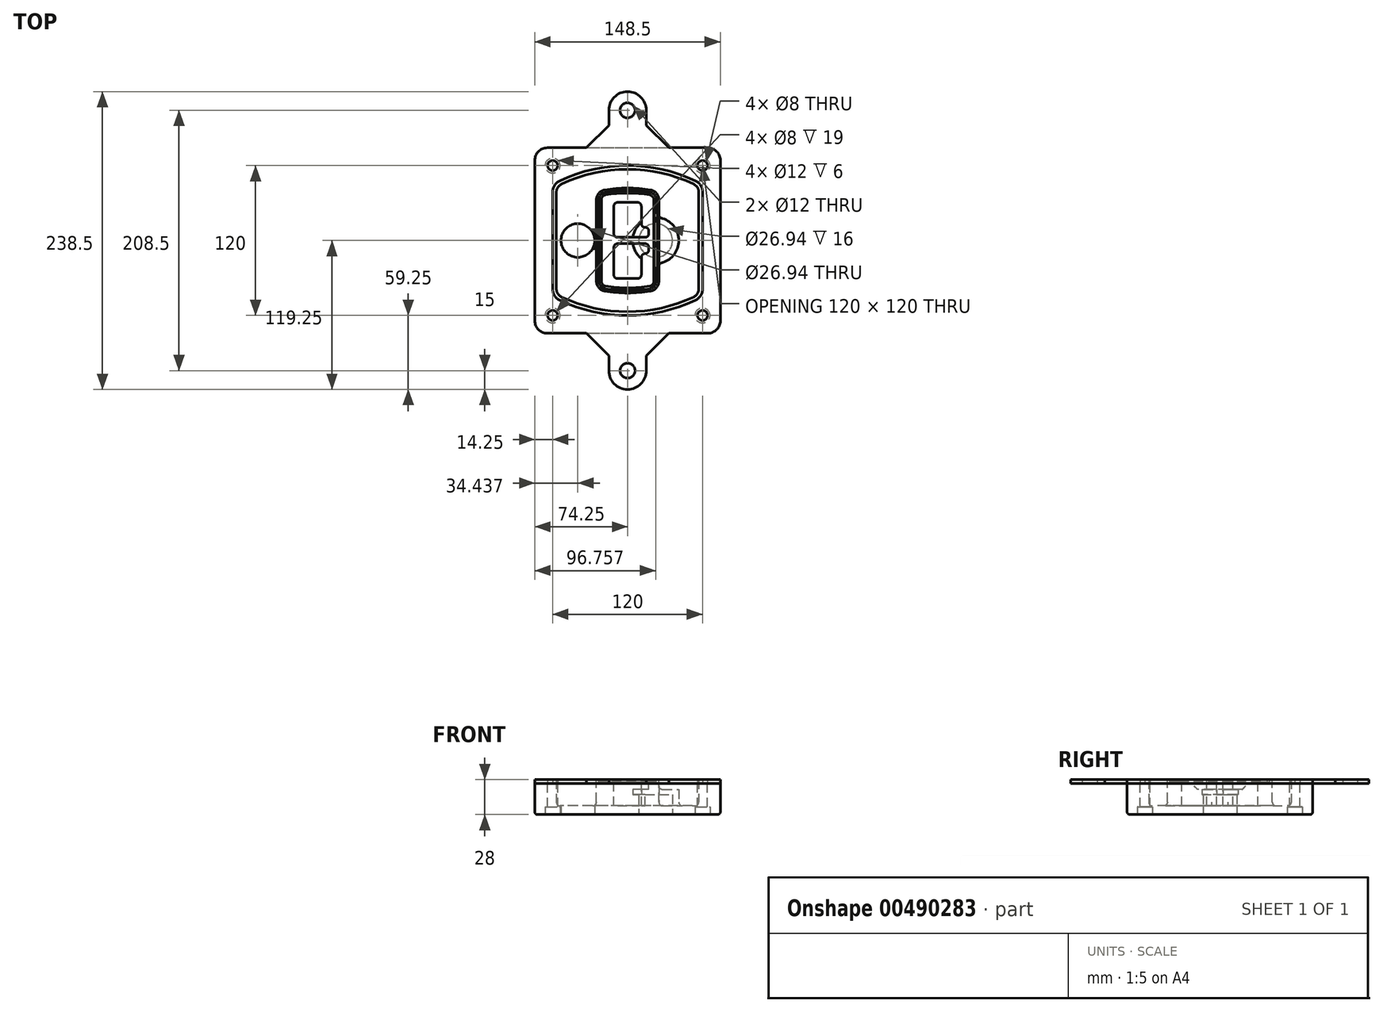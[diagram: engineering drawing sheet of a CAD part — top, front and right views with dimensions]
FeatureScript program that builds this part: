
annotation { "Feature Type Name" : "Feature", "Feature Type Description" : "" }
export const myFeature = defineFeature(function(context is Context, id is Id, definition is map)
    precondition{}
    {
        {
            var Q0;
            Q0=qCreatedBy(makeId("Top.planeOp"),FACE);
            var sketch = newSketch(context, id + "F0", { "sketchPlane" : qUnion([Q0])});
            skPoint(sketch, "E0.rect.middle", {"position": v(0, 0) * mm});
            skLineSegment(sketch, "E1.bottom", {"start": v(-64.25, -74.25) * mm, "end": v(64.25, -74.25) * mm});
            skLineSegment(sketch, "E1.top", {"start": v(-64.25, 74.25) * mm, "end": v(64.25, 74.25) * mm});
            skLineSegment(sketch, "E1.left", {"start": v(-74.25, -64.25) * mm, "end": v(-74.25, 64.25) * mm});
            skLineSegment(sketch, "E1.right", {"start": v(74.25, -64.25) * mm, "end": v(74.25, 64.25) * mm});
            skLineSegment(sketch, "E2", {"start": v(-74.25, 74.25) * mm, "end": v(74.25, -74.25) * mm, "construction": true});
            skLineSegment(sketch, "E3", {"start": v(74.25, 74.25) * mm, "end": v(-74.25, -74.25) * mm, "construction": true});
            skCircle(sketch, "E4", {"center": v(-60, 60) * mm, "radius": 4 * mm});
            skCircle(sketch, "E5", {"center": v(60, 60) * mm, "radius": 4 * mm});
            skCircle(sketch, "E6", {"center": v(60, -60) * mm, "radius": 4 * mm});
            skCircle(sketch, "E7", {"center": v(-60, -60) * mm, "radius": 4 * mm});
            skLineSegment(sketch, "E8", {"start": v(-60, 60) * mm, "end": v(60, 60) * mm, "construction": true});
            skLineSegment(sketch, "E9", {"start": v(60, 60) * mm, "end": v(60, -60) * mm, "construction": true});
            skLineSegment(sketch, "E10", {"start": v(60, -60) * mm, "end": v(-60, -60) * mm, "construction": true});
            skLineSegment(sketch, "E11", {"start": v(-60, -60) * mm, "end": v(-60, 60) * mm, "construction": true});
            skLineSegment(sketch, "E12", {"start": v(-60, 38.83) * mm, "end": v(-60, -38.83) * mm});
            skLineSegment(sketch, "E13", {"start": v(60, 38.83) * mm, "end": v(60, -38.83) * mm});
            skArc(sketch, "E14", {"start": v(54.26, 47.88) * mm, "mid": v(0, 60) * mm, "end": v(-54.26, 47.88) * mm});
            skArc(sketch, "E15", {"start": v(-54.26, -47.88) * mm, "mid": v(0, -60) * mm, "end": v(54.26, -47.88) * mm});
            skLineSegment(sketch, "E16", {"start": v(-60, 0) * mm, "end": v(60, 0) * mm, "construction": true});
            skPoint(sketch, "E17.visualSharp", {"position": v(-60, -45) * mm});
            skArc(sketch, "E17.filletArc", {"start": v(-60, -38.83) * mm, "mid": v(-58.44, -44.2) * mm, "end": v(-54.26, -47.88) * mm});
            skPoint(sketch, "E18.visualSharp", {"position": v(-60, 45) * mm});
            skArc(sketch, "E18.filletArc", {"start": v(-54.26, 47.88) * mm, "mid": v(-58.44, 44.2) * mm, "end": v(-60, 38.83) * mm});
            skPoint(sketch, "E19.visualSharp", {"position": v(60, 45) * mm});
            skArc(sketch, "E19.filletArc", {"start": v(60, 38.83) * mm, "mid": v(58.44, 44.2) * mm, "end": v(54.26, 47.88) * mm});
            skPoint(sketch, "E20.visualSharp", {"position": v(60, -45) * mm});
            skArc(sketch, "E20.filletArc", {"start": v(54.26, -47.88) * mm, "mid": v(58.44, -44.2) * mm, "end": v(60, -38.83) * mm});
            skPoint(sketch, "E21.visualSharp", {"position": v(-74.25, 74.25) * mm});
            skArc(sketch, "E21.filletArc", {"start": v(-64.25, 74.25) * mm, "mid": v(-71.32, 71.32) * mm, "end": v(-74.25, 64.25) * mm});
            skPoint(sketch, "E22.visualSharp", {"position": v(74.25, 74.25) * mm});
            skArc(sketch, "E22.filletArc", {"start": v(74.25, 64.25) * mm, "mid": v(71.32, 71.32) * mm, "end": v(64.25, 74.25) * mm});
            skPoint(sketch, "E23.visualSharp", {"position": v(74.25, -74.25) * mm});
            skArc(sketch, "E23.filletArc", {"start": v(64.25, -74.25) * mm, "mid": v(71.32, -71.32) * mm, "end": v(74.25, -64.25) * mm});
            skPoint(sketch, "E24.visualSharp", {"position": v(-74.25, -74.25) * mm});
            skArc(sketch, "E24.filletArc", {"start": v(-74.25, -64.25) * mm, "mid": v(-71.32, -71.32) * mm, "end": v(-64.25, -74.25) * mm});
            skArc(sketch, "E25.0", {"start": v(57, 38.83) * mm, "mid": v(55.9, 42.58) * mm, "end": v(52.98, 45.17) * mm});
            skLineSegment(sketch, "E25.1", {"start": v(57, 38.83) * mm, "end": v(57, -38.83) * mm});
            skArc(sketch, "E25.2", {"start": v(52.98, -45.17) * mm, "mid": v(55.9, -42.58) * mm, "end": v(57, -38.83) * mm});
            skArc(sketch, "E25.3", {"start": v(-52.98, -45.17) * mm, "mid": v(0, -57) * mm, "end": v(52.98, -45.17) * mm});
            skArc(sketch, "E25.4", {"start": v(-57, -38.83) * mm, "mid": v(-55.9, -42.58) * mm, "end": v(-52.98, -45.17) * mm});
            skArc(sketch, "E25.5", {"start": v(52.98, 45.17) * mm, "mid": v(0, 57) * mm, "end": v(-52.98, 45.17) * mm});
            skLineSegment(sketch, "E25.6", {"start": v(-57, 38.83) * mm, "end": v(-57, -38.83) * mm});
            skArc(sketch, "E25.7", {"start": v(-52.98, 45.17) * mm, "mid": v(-55.9, 42.58) * mm, "end": v(-57, 38.83) * mm});
            skArc(sketch, "E26.0", {"start": v(-55.96, 51.5) * mm, "mid": v(-61.82, 46.33) * mm, "end": v(-64, 38.83) * mm});
            skArc(sketch, "E26.1", {"start": v(55.96, 51.5) * mm, "mid": v(0, 64) * mm, "end": v(-55.96, 51.5) * mm});
            skArc(sketch, "E26.2", {"start": v(64, 38.83) * mm, "mid": v(61.82, 46.33) * mm, "end": v(55.96, 51.5) * mm});
            skLineSegment(sketch, "E26.3", {"start": v(64, 38.83) * mm, "end": v(64, -38.83) * mm});
            skArc(sketch, "E26.4", {"start": v(55.96, -51.5) * mm, "mid": v(61.82, -46.33) * mm, "end": v(64, -38.83) * mm});
            skLineSegment(sketch, "E26.5", {"start": v(-64, 38.83) * mm, "end": v(-64, -38.83) * mm});
            skArc(sketch, "E26.6", {"start": v(-55.96, -51.5) * mm, "mid": v(0, -64) * mm, "end": v(55.96, -51.5) * mm});
            skArc(sketch, "E26.7", {"start": v(-64, -38.83) * mm, "mid": v(-61.82, -46.33) * mm, "end": v(-55.96, -51.5) * mm});
            skSolve(sketch);
        }
        {
            var Q0;
            Q0=makeQuery(id+"F0.imprint","IMPRINT",FACE,{"disambiguationData":[TD([[makeQuery(id+"F0.imprint","IMPRINT",EDGE,{"derivedFrom":sQuery(id+"F0.wireOp",EDGE,"E1.bottom")}),1.0]])]});
            var Q1;
            Q1=makeQuery(id+"F0.imprint","IMPRINT",FACE,{"disambiguationData":[TD([[makeQuery(id+"F0.imprint","IMPRINT",EDGE,{"derivedFrom":sQuery(id+"F0.wireOp",EDGE,"E12")}),1.0]])]});
            var Q2;
            Q2=makeQuery(id+"F0.imprint","IMPRINT",FACE,{"disambiguationData":[TD([[makeQuery(id+"F0.imprint","IMPRINT",EDGE,{"derivedFrom":sQuery(id+"F0.wireOp",EDGE,"E25.0")}),1.0]])]});
            var Q3;
            Q3=makeQuery(id+"F0.imprint","IMPRINT",FACE,{"disambiguationData":[TD([[makeQuery(id+"F0.imprint","IMPRINT",EDGE,{"derivedFrom":sQuery(id+"F0.wireOp",EDGE,"E12")}),-1.0]])]});
            extrude(context, id + "F1", {"entities" : qUnion([Q0, Q1, Q2, Q3]), "oppositeDirection" : true, "depth" : 25 * mm});
        }
        {
            var Q0;
            Q0=makeQuery(id+"F0.imprint","IMPRINT",FACE,{"disambiguationData":[TD([[makeQuery(id+"F0.imprint","IMPRINT",EDGE,{"derivedFrom":sQuery(id+"F0.wireOp",EDGE,"E12")}),1.0]])]});
            extrude(context, id + "F2", {"entities" : qUnion([Q0]), "operationType" : NewBodyOperationType.ADD, "depth" : 3 * mm});
        }
        {
            var Q0;
            Q0=makeQuery(id+"F0.imprint","IMPRINT",FACE,{"disambiguationData":[TD([[makeQuery(id+"F0.imprint","IMPRINT",EDGE,{"derivedFrom":sQuery(id+"F0.wireOp",EDGE,"E25.0")}),1.0]])]});
            extrude(context, id + "F3", {"entities" : qUnion([Q0]), "operationType" : NewBodyOperationType.REMOVE, "oppositeDirection" : true, "depth" : 18 * mm});
        }
        {
            var Q0;
            Q0=makeQuery(id+"F2.opExtrude","CAP_FACE",FACE,{"disambiguationData":[OSD([sQuery(id+"F0.wireOp",EDGE,"E12"),sQuery(id+"F0.wireOp",EDGE,"E13"),sQuery(id+"F0.wireOp",EDGE,"E14"),sQuery(id+"F0.wireOp",EDGE,"E15"),sQuery(id+"F0.wireOp",EDGE,"E17.filletArc"),sQuery(id+"F0.wireOp",EDGE,"E18.filletArc"),sQuery(id+"F0.wireOp",EDGE,"E19.filletArc"),sQuery(id+"F0.wireOp",EDGE,"E20.filletArc"),sQuery(id+"F0.wireOp",EDGE,"E25.0"),sQuery(id+"F0.wireOp",EDGE,"E25.1"),sQuery(id+"F0.wireOp",EDGE,"E25.2"),sQuery(id+"F0.wireOp",EDGE,"E25.3"),sQuery(id+"F0.wireOp",EDGE,"E25.4"),sQuery(id+"F0.wireOp",EDGE,"E25.5"),sQuery(id+"F0.wireOp",EDGE,"E25.6"),sQuery(id+"F0.wireOp",EDGE,"E25.7")])],"isStart":false});
            var sketch = newSketch(context, id + "F4", { "sketchPlane" : qUnion([Q0])});
            skArc(sketch, "E27.0", {"start": v(-18.34, -40.45) * mm, "mid": v(0, -42) * mm, "end": v(18.34, -40.45) * mm});
            skArc(sketch, "E28.0", {"start": v(18.34, 40.45) * mm, "mid": v(0, 42) * mm, "end": v(-18.34, 40.45) * mm});
            skLineSegment(sketch, "E29", {"start": v(-25, 32.57) * mm, "end": v(-25, -32.57) * mm});
            skLineSegment(sketch, "E30", {"start": v(25, 32.57) * mm, "end": v(25, -32.57) * mm});
            skLineSegment(sketch, "E31", {"start": v(-25, 39.1) * mm, "end": v(25, 39.1) * mm, "construction": true});
            skLineSegment(sketch, "E32", {"start": v(-25, -39.1) * mm, "end": v(25, -39.1) * mm, "construction": true});
            skPoint(sketch, "E33.visualSharp", {"position": v(-25, 39.1) * mm});
            skArc(sketch, "E33.filletArc", {"start": v(-18.34, 40.45) * mm, "mid": v(-23.11, 37.73) * mm, "end": v(-25, 32.57) * mm});
            skPoint(sketch, "E34.visualSharp", {"position": v(25, 39.1) * mm});
            skArc(sketch, "E34.filletArc", {"start": v(25, 32.57) * mm, "mid": v(23.11, 37.73) * mm, "end": v(18.34, 40.45) * mm});
            skPoint(sketch, "E35.visualSharp", {"position": v(25, -39.1) * mm});
            skArc(sketch, "E35.filletArc", {"start": v(18.34, -40.45) * mm, "mid": v(23.11, -37.73) * mm, "end": v(25, -32.57) * mm});
            skPoint(sketch, "E36.visualSharp", {"position": v(-25, -39.1) * mm});
            skArc(sketch, "E36.filletArc", {"start": v(-25, -32.57) * mm, "mid": v(-23.11, -37.73) * mm, "end": v(-18.34, -40.45) * mm});
            skArc(sketch, "E37.0", {"start": v(52.98, 45.17) * mm, "mid": v(0, 57) * mm, "end": v(-52.98, 45.17) * mm});
            skArc(sketch, "E37.1", {"start": v(-52.98, 45.17) * mm, "mid": v(-55.9, 42.58) * mm, "end": v(-57, 38.83) * mm});
            skLineSegment(sketch, "E37.2", {"start": v(-57, 38.83) * mm, "end": v(-57, -38.83) * mm});
            skArc(sketch, "E37.3", {"start": v(-57, -38.83) * mm, "mid": v(-55.9, -42.58) * mm, "end": v(-52.98, -45.17) * mm});
            skArc(sketch, "E37.4", {"start": v(-52.98, -45.17) * mm, "mid": v(0, -57) * mm, "end": v(52.98, -45.17) * mm});
            skArc(sketch, "E37.5", {"start": v(52.98, -45.17) * mm, "mid": v(55.9, -42.58) * mm, "end": v(57, -38.83) * mm});
            skLineSegment(sketch, "E37.6", {"start": v(57, 38.83) * mm, "end": v(57, -38.83) * mm});
            skArc(sketch, "E37.7", {"start": v(57, 38.83) * mm, "mid": v(55.9, 42.58) * mm, "end": v(52.98, 45.17) * mm});
            skLineSegment(sketch, "E38.0", {"start": v(23, 32.57) * mm, "end": v(23, -32.57) * mm});
            skArc(sketch, "E38.1", {"start": v(18, -38.48) * mm, "mid": v(21.58, -36.44) * mm, "end": v(23, -32.57) * mm});
            skArc(sketch, "E38.2", {"start": v(-18, -38.48) * mm, "mid": v(0, -40) * mm, "end": v(18, -38.48) * mm});
            skArc(sketch, "E38.3", {"start": v(-23, -32.57) * mm, "mid": v(-21.58, -36.44) * mm, "end": v(-18, -38.48) * mm});
            skLineSegment(sketch, "E38.4", {"start": v(-23, 32.57) * mm, "end": v(-23, -32.57) * mm});
            skArc(sketch, "E38.5", {"start": v(23, 32.57) * mm, "mid": v(21.58, 36.44) * mm, "end": v(18, 38.48) * mm});
            skArc(sketch, "E38.6", {"start": v(-18, 38.48) * mm, "mid": v(-21.58, 36.44) * mm, "end": v(-23, 32.57) * mm});
            skArc(sketch, "E38.7", {"start": v(18, 38.48) * mm, "mid": v(0, 40) * mm, "end": v(-18, 38.48) * mm});
            skArc(sketch, "E39.0", {"start": v(21, 32.57) * mm, "mid": v(20.06, 35.15) * mm, "end": v(17.67, 36.5) * mm});
            skLineSegment(sketch, "E39.1", {"start": v(21, 32.57) * mm, "end": v(21, -32.57) * mm});
            skArc(sketch, "E39.2", {"start": v(17.67, -36.5) * mm, "mid": v(20.06, -35.15) * mm, "end": v(21, -32.57) * mm});
            skArc(sketch, "E39.3", {"start": v(-17.67, -36.5) * mm, "mid": v(0, -38) * mm, "end": v(17.67, -36.5) * mm});
            skArc(sketch, "E39.4", {"start": v(-21, -32.57) * mm, "mid": v(-20.06, -35.15) * mm, "end": v(-17.67, -36.5) * mm});
            skArc(sketch, "E39.5", {"start": v(17.67, 36.5) * mm, "mid": v(0, 38) * mm, "end": v(-17.67, 36.5) * mm});
            skLineSegment(sketch, "E39.6", {"start": v(-21, 32.57) * mm, "end": v(-21, -32.57) * mm});
            skArc(sketch, "E39.7", {"start": v(-17.67, 36.5) * mm, "mid": v(-20.06, 35.15) * mm, "end": v(-21, 32.57) * mm});
            skLineSegment(sketch, "E40", {"start": v(-25, 0) * mm, "end": v(25, 0) * mm, "construction": true});
            skLineSegment(sketch, "E41", {"start": v(-11, 5.5) * mm, "end": v(-11, 27.5) * mm});
            skLineSegment(sketch, "E42", {"start": v(-8, 30.5) * mm, "end": v(8, 30.5) * mm});
            skLineSegment(sketch, "E43", {"start": v(11, 27.5) * mm, "end": v(11, 13.5) * mm});
            skLineSegment(sketch, "E44", {"start": v(14, 10.5) * mm, "end": v(14, 10.5) * mm});
            skLineSegment(sketch, "E45", {"start": v(17, 7.5) * mm, "end": v(17, 5.5) * mm});
            skLineSegment(sketch, "E46", {"start": v(14, 2.5) * mm, "end": v(-8, 2.5) * mm});
            skPoint(sketch, "E47.visualSharp", {"position": v(-11, 30.5) * mm});
            skArc(sketch, "E47.filletArc", {"start": v(-8, 30.5) * mm, "mid": v(-10.12, 29.62) * mm, "end": v(-11, 27.5) * mm});
            skPoint(sketch, "E48.visualSharp", {"position": v(11, 30.5) * mm});
            skArc(sketch, "E48.filletArc", {"start": v(11, 27.5) * mm, "mid": v(10.12, 29.62) * mm, "end": v(8, 30.5) * mm});
            skPoint(sketch, "E49.visualSharp", {"position": v(11, 10.5) * mm});
            skArc(sketch, "E49.filletArc", {"start": v(11, 13.5) * mm, "mid": v(11.88, 11.38) * mm, "end": v(14, 10.5) * mm});
            skPoint(sketch, "E50.visualSharp", {"position": v(17, 10.5) * mm});
            skArc(sketch, "E50.filletArc", {"start": v(17, 7.5) * mm, "mid": v(16.12, 9.62) * mm, "end": v(14, 10.5) * mm});
            skPoint(sketch, "E51.visualSharp", {"position": v(17, 2.5) * mm});
            skArc(sketch, "E51.filletArc", {"start": v(14, 2.5) * mm, "mid": v(16.12, 3.38) * mm, "end": v(17, 5.5) * mm});
            skPoint(sketch, "E52.visualSharp", {"position": v(-11, 2.5) * mm});
            skArc(sketch, "E52.filletArc", {"start": v(-11, 5.5) * mm, "mid": v(-10.12, 3.38) * mm, "end": v(-8, 2.5) * mm});
            skLineSegment(sketch, "E53.0.MirrorCS", {"start": v(14, -2.5) * mm, "end": v(-8, -2.5) * mm});
            skArc(sketch, "E54.0.MirrorCS", {"start": v(-11, -5.5) * mm, "mid": v(-10.12, -3.38) * mm, "end": v(-8, -2.5) * mm});
            skLineSegment(sketch, "E55.0.MirrorCS", {"start": v(-11, -5.5) * mm, "end": v(-11, -27.5) * mm});
            skArc(sketch, "E56.0.MirrorCS", {"start": v(-8, -30.5) * mm, "mid": v(-10.12, -29.62) * mm, "end": v(-11, -27.5) * mm});
            skLineSegment(sketch, "E57.0.MirrorCS", {"start": v(-8, -30.5) * mm, "end": v(8, -30.5) * mm});
            skArc(sketch, "E58.0.MirrorCS", {"start": v(11, -27.5) * mm, "mid": v(10.12, -29.62) * mm, "end": v(8, -30.5) * mm});
            skLineSegment(sketch, "E59.0.MirrorCS", {"start": v(11, -27.5) * mm, "end": v(11, -13.5) * mm});
            skArc(sketch, "E60.0.MirrorCS", {"start": v(11, -13.5) * mm, "mid": v(11.88, -11.38) * mm, "end": v(14, -10.5) * mm});
            skArc(sketch, "E61.0.MirrorCS", {"start": v(17, -7.5) * mm, "mid": v(16.12, -9.62) * mm, "end": v(14, -10.5) * mm});
            skLineSegment(sketch, "E62.0.MirrorCS", {"start": v(17, -7.5) * mm, "end": v(17, -5.5) * mm});
            skArc(sketch, "E63.0.MirrorCS", {"start": v(14, -2.5) * mm, "mid": v(16.12, -3.38) * mm, "end": v(17, -5.5) * mm});
            skSolve(sketch);
        }
        {
            var Q0;
            Q0=makeQuery(id+"F4.imprint","IMPRINT",FACE,{"disambiguationData":[TD([[makeQuery(id+"F4.imprint","IMPRINT",EDGE,{"derivedFrom":sQuery(id+"F4.wireOp",EDGE,"E27.0")}),1.0]])]});
            var Q1;
            Q1=makeQuery(id+"F4.imprint","IMPRINT",FACE,{"disambiguationData":[TD([[makeQuery(id+"F4.imprint","IMPRINT",EDGE,{"derivedFrom":sQuery(id+"F4.wireOp",EDGE,"E38.0")}),-1.0]])]});
            var Q2;
            Q2=makeQuery(id+"F4.imprint","IMPRINT",FACE,{"disambiguationData":[TD([[makeQuery(id+"F4.imprint","IMPRINT",EDGE,{"derivedFrom":sQuery(id+"F4.wireOp",EDGE,"E39.0")}),1.0]])]});
            extrude(context, id + "F5", {"entities" : qUnion([Q0, Q1, Q2]), "operationType" : NewBodyOperationType.ADD, "endBound" : BoundingType.UP_TO_NEXT, "oppositeDirection" : true, "depth" : 25 * mm});
        }
        {
            var Q0;
            Q0=makeQuery(id+"F4.imprint","IMPRINT",FACE,{"disambiguationData":[TD([[makeQuery(id+"F4.imprint","IMPRINT",EDGE,{"derivedFrom":sQuery(id+"F4.wireOp",EDGE,"E38.0")}),-1.0]])]});
            extrude(context, id + "F6", {"entities" : qUnion([Q0]), "operationType" : NewBodyOperationType.REMOVE, "oppositeDirection" : true, "depth" : 2 * mm});
        }
        {
            var Q0;
            Q0=makeQuery(id+"F1.opExtrude","CAP_FACE",FACE,{"disambiguationData":[OSD([sQuery(id+"F0.wireOp",EDGE,"E1.bottom"),sQuery(id+"F0.wireOp",EDGE,"E1.top"),sQuery(id+"F0.wireOp",EDGE,"E1.left"),sQuery(id+"F0.wireOp",EDGE,"E1.right"),sQuery(id+"F0.wireOp",EDGE,"E4"),sQuery(id+"F0.wireOp",EDGE,"E5"),sQuery(id+"F0.wireOp",EDGE,"E6"),sQuery(id+"F0.wireOp",EDGE,"E7"),sQuery(id+"F0.wireOp",EDGE,"E21.filletArc"),sQuery(id+"F0.wireOp",EDGE,"E22.filletArc"),sQuery(id+"F0.wireOp",EDGE,"E23.filletArc"),sQuery(id+"F0.wireOp",EDGE,"E24.filletArc")])],"isStart":false});
            var sketch = newSketch(context, id + "F7", { "sketchPlane" : qUnion([Q0])});
            skCircle(sketch, "E64", {"center": v(22.5, 0) * mm, "radius": 13.47 * mm});
            skCircle(sketch, "E65", {"center": v(-39.81, 0) * mm, "radius": 13.47 * mm});
            skLineSegment(sketch, "E66", {"start": v(74.25, 0) * mm, "end": v(-74.25, 0) * mm});
            skCircle(sketch, "E67", {"center": v(22.5, 0) * mm, "radius": 18.47 * mm});
            skCircle(sketch, "E68", {"center": v(60, -60) * mm, "radius": 6 * mm});
            skCircle(sketch, "E69", {"center": v(-60, -60) * mm, "radius": 6 * mm});
            skCircle(sketch, "E70", {"center": v(-60, 60) * mm, "radius": 6 * mm});
            skCircle(sketch, "E71", {"center": v(60, 60) * mm, "radius": 6 * mm});
            skSolve(sketch);
        }
        {
            var Q0;
            {var subQ1=sQuery(id+"F7.wireOp",EDGE,"E66");var subQ4=sQuery(id+"F7.wireOp",EDGE,"E64");var subQ6=makeQuery(id+"F7.imprint","INTERSECT",VERTEX,{"disambiguationData":[OD(0.0)],"derivedFrom":[subQ4,subQ1]});Q0=makeQuery(id+"F7.imprint","IMPRINT",FACE,{"disambiguationData":[TD([[makeQuery(id+"F7.imprint","IMPRINT",EDGE,{"disambiguationData":[TD([[subQ6,-1.0]])],"derivedFrom":subQ4}),-1.0]])]});}
            var Q1;
            {var subQ0=sQuery(id+"F7.wireOp",EDGE,"E66");var subQ1=sQuery(id+"F7.wireOp",EDGE,"E64");var subQ3=makeQuery(id+"F7.imprint","INTERSECT",VERTEX,{"disambiguationData":[OD(0.0)],"derivedFrom":[subQ1,subQ0]});Q1=makeQuery(id+"F7.imprint","IMPRINT",FACE,{"disambiguationData":[TD([[makeQuery(id+"F7.imprint","IMPRINT",EDGE,{"disambiguationData":[TD([[subQ3,-1.0]])],"derivedFrom":subQ1}),1.0]])]});}
            var Q2;
            {var subQ0=sQuery(id+"F7.wireOp",EDGE,"E66");var subQ1=sQuery(id+"F7.wireOp",EDGE,"E64");var subQ3=makeQuery(id+"F7.imprint","INTERSECT",VERTEX,{"disambiguationData":[OD(0.0)],"derivedFrom":[subQ1,subQ0]});Q2=makeQuery(id+"F7.imprint","IMPRINT",FACE,{"disambiguationData":[TD([[makeQuery(id+"F7.imprint","IMPRINT",EDGE,{"disambiguationData":[TD([[subQ3,1.0]])],"derivedFrom":subQ1}),1.0]])]});}
            var Q3;
            {var subQ1=sQuery(id+"F7.wireOp",EDGE,"E66");var subQ4=sQuery(id+"F7.wireOp",EDGE,"E64");var subQ6=makeQuery(id+"F7.imprint","INTERSECT",VERTEX,{"disambiguationData":[OD(0.0)],"derivedFrom":[subQ4,subQ1]});Q3=makeQuery(id+"F7.imprint","IMPRINT",FACE,{"disambiguationData":[TD([[makeQuery(id+"F7.imprint","IMPRINT",EDGE,{"disambiguationData":[TD([[subQ6,1.0]])],"derivedFrom":subQ4}),-1.0]])]});}
            extrude(context, id + "F8", {"entities" : qUnion([Q0, Q1, Q2, Q3]), "operationType" : NewBodyOperationType.ADD, "oppositeDirection" : true, "depth" : 20 * mm});
        }
        {
            var Q0;
            {var subQ0=sQuery(id+"F7.wireOp",EDGE,"E66");var subQ1=sQuery(id+"F7.wireOp",EDGE,"E64");var subQ3=makeQuery(id+"F7.imprint","INTERSECT",VERTEX,{"disambiguationData":[OD(0.0)],"derivedFrom":[subQ1,subQ0]});Q0=makeQuery(id+"F7.imprint","IMPRINT",FACE,{"disambiguationData":[TD([[makeQuery(id+"F7.imprint","IMPRINT",EDGE,{"disambiguationData":[TD([[subQ3,-1.0]])],"derivedFrom":subQ1}),1.0]])]});}
            var Q1;
            {var subQ0=sQuery(id+"F7.wireOp",EDGE,"E66");var subQ1=sQuery(id+"F7.wireOp",EDGE,"E64");var subQ3=makeQuery(id+"F7.imprint","INTERSECT",VERTEX,{"disambiguationData":[OD(0.0)],"derivedFrom":[subQ1,subQ0]});Q1=makeQuery(id+"F7.imprint","IMPRINT",FACE,{"disambiguationData":[TD([[makeQuery(id+"F7.imprint","IMPRINT",EDGE,{"disambiguationData":[TD([[subQ3,1.0]])],"derivedFrom":subQ1}),1.0]])]});}
            extrude(context, id + "F9", {"entities" : qUnion([Q0, Q1]), "operationType" : NewBodyOperationType.REMOVE, "oppositeDirection" : true, "depth" : 16 * mm});
        }
        {
            var Q0;
            {var subQ0=sQuery(id+"F7.wireOp",EDGE,"E66");var subQ1=sQuery(id+"F7.wireOp",EDGE,"E65");var subQ3=makeQuery(id+"F7.imprint","INTERSECT",VERTEX,{"disambiguationData":[OD(0.0)],"derivedFrom":[subQ1,subQ0]});Q0=makeQuery(id+"F7.imprint","IMPRINT",FACE,{"disambiguationData":[TD([[makeQuery(id+"F7.imprint","IMPRINT",EDGE,{"disambiguationData":[TD([[subQ3,-1.0]])],"derivedFrom":subQ1}),1.0]])]});}
            var Q1;
            {var subQ0=sQuery(id+"F7.wireOp",EDGE,"E66");var subQ1=sQuery(id+"F7.wireOp",EDGE,"E65");var subQ3=makeQuery(id+"F7.imprint","INTERSECT",VERTEX,{"disambiguationData":[OD(0.0)],"derivedFrom":[subQ1,subQ0]});Q1=makeQuery(id+"F7.imprint","IMPRINT",FACE,{"disambiguationData":[TD([[makeQuery(id+"F7.imprint","IMPRINT",EDGE,{"disambiguationData":[TD([[subQ3,1.0]])],"derivedFrom":subQ1}),1.0]])]});}
            extrude(context, id + "F10", {"entities" : qUnion([Q0, Q1]), "operationType" : NewBodyOperationType.REMOVE, "oppositeDirection" : true, "depth" : 25 * mm});
        }
        {
            var Q0;
            Q0=makeQuery(id+"F7.imprint","IMPRINT",FACE,{"disambiguationData":[TD([[makeQuery(id+"F7.imprint","IMPRINT",EDGE,{"derivedFrom":sQuery(id+"F7.wireOp",EDGE,"E68")}),1.0]])]});
            var Q1;
            Q1=makeQuery(id+"F7.imprint","IMPRINT",FACE,{"disambiguationData":[TD([[makeQuery(id+"F7.imprint","IMPRINT",EDGE,{"derivedFrom":makeQuery(id+"F1.opExtrude","CAP_EDGE",EDGE,{"disambiguationData":[OSD([sQuery(id+"F0.wireOp",EDGE,"E5")])],"isStart":false})}),-1.0]])]});
            var Q2;
            Q2=makeQuery(id+"F7.imprint","IMPRINT",FACE,{"disambiguationData":[TD([[makeQuery(id+"F7.imprint","IMPRINT",EDGE,{"derivedFrom":sQuery(id+"F7.wireOp",EDGE,"E69")}),1.0]])]});
            var Q3;
            Q3=makeQuery(id+"F7.imprint","IMPRINT",FACE,{"disambiguationData":[TD([[makeQuery(id+"F7.imprint","IMPRINT",EDGE,{"derivedFrom":makeQuery(id+"F1.opExtrude","CAP_EDGE",EDGE,{"disambiguationData":[OSD([sQuery(id+"F0.wireOp",EDGE,"E4")])],"isStart":false})}),-1.0]])]});
            var Q4;
            Q4=makeQuery(id+"F7.imprint","IMPRINT",FACE,{"disambiguationData":[TD([[makeQuery(id+"F7.imprint","IMPRINT",EDGE,{"derivedFrom":sQuery(id+"F7.wireOp",EDGE,"E70")}),1.0]])]});
            var Q5;
            Q5=makeQuery(id+"F7.imprint","IMPRINT",FACE,{"disambiguationData":[TD([[makeQuery(id+"F7.imprint","IMPRINT",EDGE,{"derivedFrom":makeQuery(id+"F1.opExtrude","CAP_EDGE",EDGE,{"disambiguationData":[OSD([sQuery(id+"F0.wireOp",EDGE,"E7")])],"isStart":false})}),-1.0]])]});
            var Q6;
            Q6=makeQuery(id+"F7.imprint","IMPRINT",FACE,{"disambiguationData":[TD([[makeQuery(id+"F7.imprint","IMPRINT",EDGE,{"derivedFrom":sQuery(id+"F7.wireOp",EDGE,"E71")}),1.0]])]});
            var Q7;
            Q7=makeQuery(id+"F7.imprint","IMPRINT",FACE,{"disambiguationData":[TD([[makeQuery(id+"F7.imprint","IMPRINT",EDGE,{"derivedFrom":makeQuery(id+"F1.opExtrude","CAP_EDGE",EDGE,{"disambiguationData":[OSD([sQuery(id+"F0.wireOp",EDGE,"E6")])],"isStart":false})}),-1.0]])]});
            extrude(context, id + "F11", {"entities" : qUnion([Q0, Q1, Q2, Q3, Q4, Q5, Q6, Q7]), "operationType" : NewBodyOperationType.REMOVE, "oppositeDirection" : true, "depth" : 6 * mm});
        }
        {
            var Q0;
            Q0=makeQuery(id+"F9.boolean.opBoolean","COPY",FACE,{"derivedFrom":makeQuery(id+"F9.opExtrude","CAP_FACE",FACE,{"disambiguationData":[OSD([sQuery(id+"F7.wireOp",EDGE,"E64")])],"isStart":false})});
            var sketch = newSketch(context, id + "F12", { "sketchPlane" : qUnion([Q0])});
            skArc(sketch, "E72.0", {"start": v(11, 14.45) * mm, "mid": v(6.45, 9.13) * mm, "end": v(4.2, 2.5) * mm});
            skArc(sketch, "E72.1", {"start": v(4.2, -2.5) * mm, "mid": v(6.45, -9.13) * mm, "end": v(11, -14.45) * mm});
            skLineSegment(sketch, "E73", {"start": v(4.2, -2.5) * mm, "end": v(14, -2.5) * mm});
            skLineSegment(sketch, "E74.0", {"start": v(14, 2.5) * mm, "end": v(4.2, 2.5) * mm});
            skArc(sketch, "E74.1", {"start": v(14, 2.5) * mm, "mid": v(16.12, 3.38) * mm, "end": v(17, 5.5) * mm});
            skLineSegment(sketch, "E74.2", {"start": v(17, 7.5) * mm, "end": v(17, 5.5) * mm});
            skArc(sketch, "E74.3", {"start": v(17, 7.5) * mm, "mid": v(16.12, 9.62) * mm, "end": v(14, 10.5) * mm});
            skArc(sketch, "E74.4", {"start": v(11, 13.5) * mm, "mid": v(11.88, 11.38) * mm, "end": v(14, 10.5) * mm});
            skLineSegment(sketch, "E74.5", {"start": v(11, 14.45) * mm, "end": v(11, 13.5) * mm});
            skLineSegment(sketch, "E74.7", {"start": v(14, -2.5) * mm, "end": v(4.2, -2.5) * mm});
            skArc(sketch, "E74.8", {"start": v(14, -2.5) * mm, "mid": v(16.12, -3.38) * mm, "end": v(17, -5.5) * mm});
            skLineSegment(sketch, "E74.9", {"start": v(17, -7.5) * mm, "end": v(17, -5.5) * mm});
            skArc(sketch, "E74.10", {"start": v(17, -7.5) * mm, "mid": v(16.12, -9.62) * mm, "end": v(14, -10.5) * mm});
            skArc(sketch, "E74.11", {"start": v(11, -13.5) * mm, "mid": v(11.88, -11.38) * mm, "end": v(14, -10.5) * mm});
            skLineSegment(sketch, "E74.12", {"start": v(11, -14.45) * mm, "end": v(11, -13.5) * mm});
            skPoint(sketch, "E75.orphan", {"position": v(11, -27.5) * mm});
            skPoint(sketch, "E76.orphan", {"position": v(-8, -2.5) * mm});
            skPoint(sketch, "E77.orphan", {"position": v(-8, 2.5) * mm});
            skPoint(sketch, "E78.orphan", {"position": v(11, 27.5) * mm});
            skSolve(sketch);
        }
        {
            var Q0;
            {var subQ7=sQuery(id+"F12.wireOp",EDGE,"E72.0");var subQ14=sQuery(id+"F12.wireOp",EDGE,"E72.1");var subQ16=sQuery(id+"F12.wireOp",EDGE,"E74.1");var subQ18=sQuery(id+"F12.wireOp",EDGE,"E74.8");Q0=qUnion([makeQuery(id+"F12.imprint","IMPRINT",FACE,{"disambiguationData":[TD([[makeQuery(id+"F12.imprint","IMPRINT",EDGE,{"derivedFrom":subQ7}),1.0]])]}),makeQuery(id+"F12.imprint","IMPRINT",FACE,{"disambiguationData":[TD([[makeQuery(id+"F12.imprint","IMPRINT",EDGE,{"derivedFrom":subQ14}),1.0]])]}),makeQuery(id+"F12.imprint","IMPRINT",FACE,{"disambiguationData":[TD([[makeQuery(id+"F12.imprint","IMPRINT",EDGE,{"derivedFrom":subQ16}),1.0]])]}),makeQuery(id+"F12.imprint","IMPRINT",FACE,{"disambiguationData":[TD([[makeQuery(id+"F12.imprint","IMPRINT",EDGE,{"derivedFrom":subQ18}),-1.0]])]})]);}
            var Q1;
            Q1=makeQuery(id+"F5.boolean.opBoolean","SPLIT",FACE,{"disambiguationData":[TD([makeQuery(id+"F5.opExtrude","SWEPT_FACE",FACE,{"disambiguationData":[OSD([sQuery(id+"F4.wireOp",EDGE,"E41")])]})])],"derivedFrom":makeQuery(id+"F3.boolean.opBoolean","COPY",FACE,{"derivedFrom":makeQuery(id+"F3.opExtrude","CAP_FACE",FACE,{"disambiguationData":[OSD([sQuery(id+"F0.wireOp",EDGE,"E25.0"),sQuery(id+"F0.wireOp",EDGE,"E25.1"),sQuery(id+"F0.wireOp",EDGE,"E25.2"),sQuery(id+"F0.wireOp",EDGE,"E25.3"),sQuery(id+"F0.wireOp",EDGE,"E25.4"),sQuery(id+"F0.wireOp",EDGE,"E25.5"),sQuery(id+"F0.wireOp",EDGE,"E25.6"),sQuery(id+"F0.wireOp",EDGE,"E25.7")])],"isStart":false})})});
            extrude(context, id + "F13", {"entities" : qUnion([Q0]), "operationType" : NewBodyOperationType.REMOVE, "endBound" : BoundingType.UP_TO_SURFACE, "endBoundEntityFace" : qUnion([Q1]), "depth" : 25 * mm});
        }
        {
            var Q0;
            Q0=makeQuery(id+"F3.boolean.opBoolean","COPY",EDGE,{"derivedFrom":makeQuery(id+"F3.opExtrude","CAP_EDGE",EDGE,{"disambiguationData":[OSD([sQuery(id+"F0.wireOp",EDGE,"E25.6")])],"isStart":false})});
            var Q1;
            Q1=makeQuery(id+"F8.boolean.opBoolean","INTERSECT",EDGE,{"derivedFrom":[makeQuery(id+"F5.opExtrude","SWEPT_FACE",FACE,{"disambiguationData":[OSD([sQuery(id+"F4.wireOp",EDGE,"E30")])]}),makeQuery(id+"F8.opExtrude","CAP_FACE",FACE,{"disambiguationData":[OSD([sQuery(id+"F7.wireOp",EDGE,"E67")])],"isStart":false})]});
            var Q2;
            Q2=makeQuery(id+"F8.boolean.opBoolean","INTERSECT",EDGE,{"disambiguationData":[OD(1.0)],"derivedFrom":[makeQuery(id+"F5.opExtrude","SWEPT_FACE",FACE,{"disambiguationData":[OSD([sQuery(id+"F4.wireOp",EDGE,"E30")])]}),makeQuery(id+"F8.opExtrude","SWEPT_FACE",FACE,{"disambiguationData":[OSD([sQuery(id+"F7.wireOp",EDGE,"E67")])]})]});
            var Q3;
            {var subQ0=sQuery(id+"F4.wireOp",EDGE,"E30");Q3=makeQuery(id+"F8.boolean.opBoolean","SPLIT",EDGE,{"disambiguationData":[TD([makeQuery(id+"F5.opExtrude","SWEPT_FACE",FACE,{"disambiguationData":[OSD([sQuery(id+"F4.wireOp",EDGE,"E35.filletArc")])]})])],"derivedFrom":makeQuery(id+"F5.opExtrude","CAP_EDGE",EDGE,{"disambiguationData":[OSD([subQ0])],"isStart":false})});}
            var Q4;
            {var subQ0=sQuery(id+"F0.wireOp",EDGE,"E25.7");var subQ1=sQuery(id+"F0.wireOp",EDGE,"E25.1");var subQ2=sQuery(id+"F0.wireOp",EDGE,"E25.6");var subQ3=sQuery(id+"F0.wireOp",EDGE,"E25.5");var subQ4=sQuery(id+"F0.wireOp",EDGE,"E25.4");var subQ5=sQuery(id+"F0.wireOp",EDGE,"E25.0");var subQ6=sQuery(id+"F0.wireOp",EDGE,"E25.2");var subQ7=sQuery(id+"F0.wireOp",EDGE,"E25.3");Q4=makeQuery(id+"F8.boolean.opBoolean","INTERSECT",EDGE,{"derivedFrom":[makeQuery(id+"F5.boolean.opBoolean","SPLIT",FACE,{"disambiguationData":[TD([makeQuery(id+"F2.opExtrude","SWEPT_FACE",FACE,{"disambiguationData":[OSD([subQ5])]})])],"derivedFrom":makeQuery(id+"F3.boolean.opBoolean","COPY",FACE,{"derivedFrom":makeQuery(id+"F3.opExtrude","CAP_FACE",FACE,{"disambiguationData":[OSD([subQ5,subQ1,subQ6,subQ7,subQ4,subQ3,subQ2,subQ0])],"isStart":false})})}),makeQuery(id+"F8.opExtrude","SWEPT_FACE",FACE,{"disambiguationData":[OSD([sQuery(id+"F7.wireOp",EDGE,"E67")])]})]});}
            var Q5;
            Q5=makeQuery(id+"F8.boolean.opBoolean","INTERSECT",EDGE,{"disambiguationData":[OD(0.0)],"derivedFrom":[makeQuery(id+"F5.opExtrude","SWEPT_FACE",FACE,{"disambiguationData":[OSD([sQuery(id+"F4.wireOp",EDGE,"E30")])]}),makeQuery(id+"F8.opExtrude","SWEPT_FACE",FACE,{"disambiguationData":[OSD([sQuery(id+"F7.wireOp",EDGE,"E67")])]})]});
            fillet(context, id + "F14", {"entities" : qUnion([Q0, Q1, Q2, Q3, Q4, Q5]), "radius" : 3 * mm, "tangentPropagation" : true, "allowEdgeOverflow" : false});
        }
        {
            var Q0;
            Q0=makeQuery(id+"F1.opExtrude","CAP_EDGE",EDGE,{"disambiguationData":[OSD([sQuery(id+"F0.wireOp",EDGE,"E1.bottom")])],"isStart":false});
            fillet(context, id + "F15", {"entities" : qUnion([Q0]), "radius" : 2 * mm, "tangentPropagation" : true, "allowEdgeOverflow" : false});
        }
        {
            var Q0;
            {var subQ0=sQuery(id+"F0.wireOp",EDGE,"E21.filletArc");var subQ1=sQuery(id+"F0.wireOp",EDGE,"E7");var subQ2=sQuery(id+"F0.wireOp",EDGE,"E6");var subQ3=sQuery(id+"F0.wireOp",EDGE,"E5");var subQ4=sQuery(id+"F0.wireOp",EDGE,"E4");var subQ5=sQuery(id+"F0.wireOp",EDGE,"E22.filletArc");var subQ6=sQuery(id+"F0.wireOp",EDGE,"E1.bottom");var subQ7=sQuery(id+"F0.wireOp",EDGE,"E1.right");var subQ8=sQuery(id+"F0.wireOp",EDGE,"E1.top");var subQ9=sQuery(id+"F0.wireOp",EDGE,"E1.left");var subQ10=sQuery(id+"F0.wireOp",EDGE,"E23.filletArc");var subQ11=sQuery(id+"F0.wireOp",EDGE,"E24.filletArc");Q0=makeQuery(id+"F2.boolean.opBoolean","SPLIT",FACE,{"disambiguationData":[TD([makeQuery(id+"F1.opExtrude","SWEPT_FACE",FACE,{"disambiguationData":[OSD([subQ6])]})])],"derivedFrom":makeQuery(id+"F1.opExtrude","CAP_FACE",FACE,{"disambiguationData":[OSD([subQ6,subQ8,subQ9,subQ7,subQ4,subQ3,subQ2,subQ1,subQ0,subQ5,subQ10,subQ11])],"isStart":true})});}
            var sketch = newSketch(context, id + "F16", { "sketchPlane" : qUnion([Q0])});
            skLineSegment(sketch, "E79", {"start": v(0, 74.25) * mm, "end": v(0, 104.25) * mm, "construction": true});
            skArc(sketch, "E80", {"start": v(15, 104.25) * mm, "mid": v(0, 119.25) * mm, "end": v(-15, 104.25) * mm});
            skLineSegment(sketch, "E81", {"start": v(15, 104.25) * mm, "end": v(15, 92.25) * mm});
            skLineSegment(sketch, "E82", {"start": v(-15, 104.25) * mm, "end": v(-15, 92.25) * mm});
            skLineSegment(sketch, "E83", {"start": v(15, 92.25) * mm, "end": v(33, 74.25) * mm});
            skLineSegment(sketch, "E84", {"start": v(-15, 92.25) * mm, "end": v(-33, 74.25) * mm});
            skCircle(sketch, "E85", {"center": v(0, 104.25) * mm, "radius": 6 * mm});
            skLineSegment(sketch, "E86", {"start": v(-74.25, 0) * mm, "end": v(74.25, 0) * mm, "construction": true});
            skLineSegment(sketch, "E87.MirrorCS", {"start": v(0, -74.25) * mm, "end": v(0, -104.25) * mm, "construction": true});
            skLineSegment(sketch, "E88.MirrorCS", {"start": v(15, -104.25) * mm, "end": v(15, -92.25) * mm});
            skLineSegment(sketch, "E89.MirrorCS", {"start": v(-15, -104.25) * mm, "end": v(-15, -92.25) * mm});
            skLineSegment(sketch, "E90.MirrorCS", {"start": v(-15, -92.25) * mm, "end": v(-33, -74.25) * mm});
            skLineSegment(sketch, "E91.MirrorCS", {"start": v(15, -92.25) * mm, "end": v(33, -74.25) * mm});
            skArc(sketch, "E92.MirrorCS", {"start": v(15, -104.25) * mm, "mid": v(0, -119.25) * mm, "end": v(-15, -104.25) * mm});
            skCircle(sketch, "E93.MirrorC", {"center": v(0, -104.25) * mm, "radius": 6 * mm});
            skSolve(sketch);
        }
        {
            var Q0;
            Q0=makeQuery(id+"F16.imprint","IMPRINT",FACE,{"disambiguationData":[TD([[makeQuery(id+"F16.imprint","IMPRINT",EDGE,{"derivedFrom":sQuery(id+"F16.wireOp",EDGE,"E80")}),1.0]])]});
            var Q1;
            Q1=makeQuery(id+"F16.imprint","IMPRINT",FACE,{"disambiguationData":[TD([[makeQuery(id+"F16.imprint","IMPRINT",EDGE,{"derivedFrom":sQuery(id+"F16.wireOp",EDGE,"E88.MirrorCS")}),1.0]])]});
            var Q2;
            Q2=makeQuery(id+"F16.imprint","IMPRINT",FACE,{"disambiguationData":[TD([[makeQuery(id+"F16.imprint","IMPRINT",EDGE,{"derivedFrom":makeQuery(id+"F1.opExtrude","CAP_EDGE",EDGE,{"disambiguationData":[OSD([sQuery(id+"F0.wireOp",EDGE,"E1.left")])],"isStart":true})}),-1.0]])]});
            var Q3;
            Q3=makeQuery(id+"F2.opExtrude","CAP_FACE",FACE,{"disambiguationData":[OSD([sQuery(id+"F0.wireOp",EDGE,"E12"),sQuery(id+"F0.wireOp",EDGE,"E13"),sQuery(id+"F0.wireOp",EDGE,"E14"),sQuery(id+"F0.wireOp",EDGE,"E15"),sQuery(id+"F0.wireOp",EDGE,"E17.filletArc"),sQuery(id+"F0.wireOp",EDGE,"E18.filletArc"),sQuery(id+"F0.wireOp",EDGE,"E19.filletArc"),sQuery(id+"F0.wireOp",EDGE,"E20.filletArc"),sQuery(id+"F0.wireOp",EDGE,"E25.0"),sQuery(id+"F0.wireOp",EDGE,"E25.1"),sQuery(id+"F0.wireOp",EDGE,"E25.2"),sQuery(id+"F0.wireOp",EDGE,"E25.3"),sQuery(id+"F0.wireOp",EDGE,"E25.4"),sQuery(id+"F0.wireOp",EDGE,"E25.5"),sQuery(id+"F0.wireOp",EDGE,"E25.6"),sQuery(id+"F0.wireOp",EDGE,"E25.7")])],"isStart":false});
            extrude(context, id + "F17", {"entities" : qUnion([Q0, Q1, Q2]), "endBound" : BoundingType.UP_TO_SURFACE, "endBoundEntityFace" : qUnion([Q3]), "depth" : 25 * mm});
        }
    });
